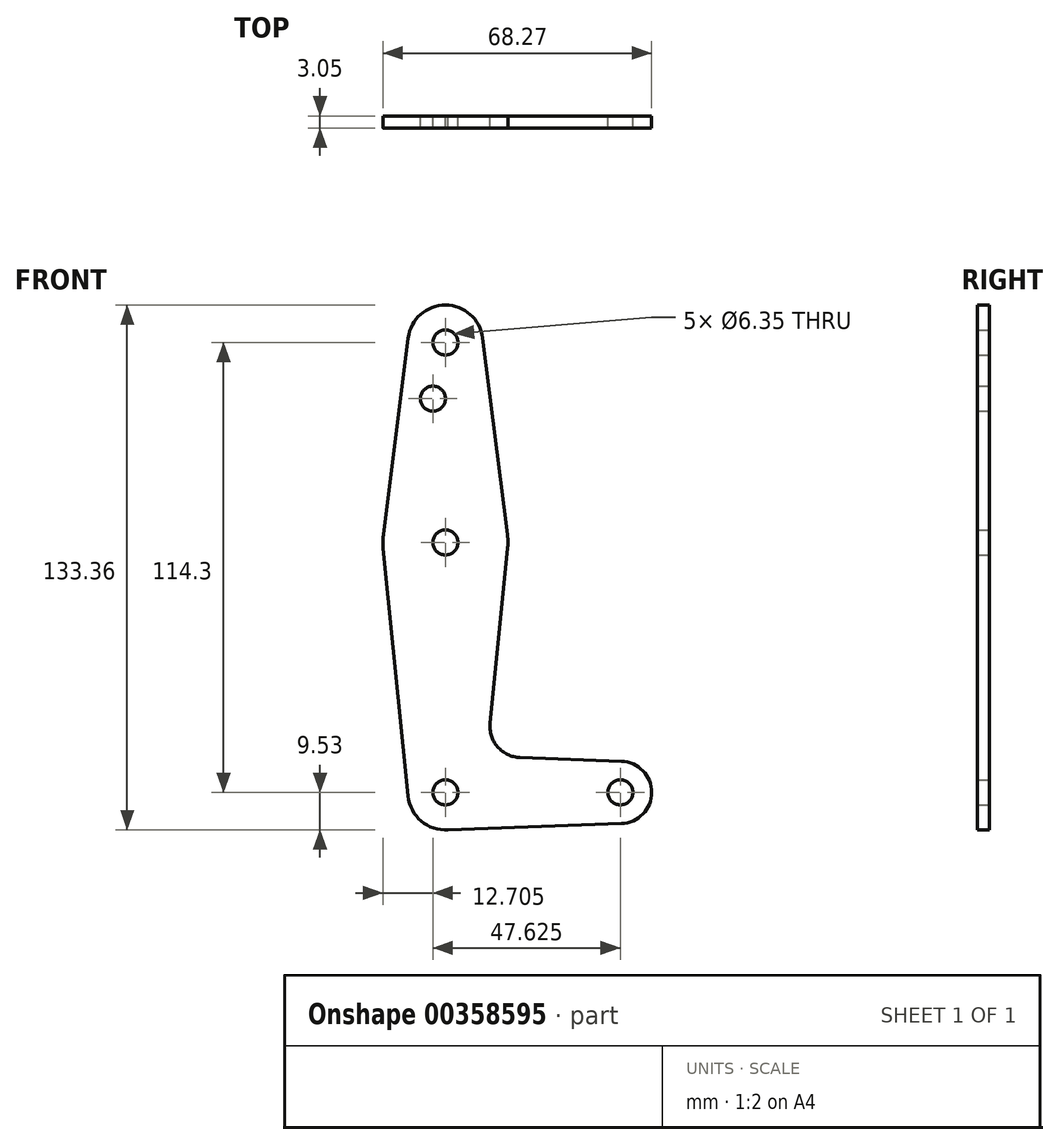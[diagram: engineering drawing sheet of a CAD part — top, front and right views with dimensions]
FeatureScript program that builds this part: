
annotation { "Feature Type Name" : "Feature", "Feature Type Description" : "" }
export const myFeature = defineFeature(function(context is Context, id is Id, definition is map)
    precondition{}
    {
        {
            var Q0;
            Q0=qCreatedBy(makeId("Front.planeOp"),FACE);
            var sketch = newSketch(context, id + "F0", { "sketchPlane" : qUnion([Q0])});
            skLineSegment(sketch, "E0", {"start": v(0, 114.3) * mm, "end": v(0, 0) * mm, "construction": true});
            skLineSegment(sketch, "E1", {"start": v(0, 0) * mm, "end": v(44.45, 0) * mm, "construction": true});
            skCircle(sketch, "E2", {"center": v(0, 114.3) * mm, "radius": 9.53 * mm});
            skCircle(sketch, "E3", {"center": v(0, 63.5) * mm, "radius": 15.88 * mm});
            skCircle(sketch, "E4", {"center": v(0, 0) * mm, "radius": 9.53 * mm});
            skCircle(sketch, "E5", {"center": v(44.45, 0) * mm, "radius": 7.94 * mm});
            skLineSegment(sketch, "E6", {"start": v(-9.45, 115.5) * mm, "end": v(-15.75, 65.48) * mm});
            skLineSegment(sketch, "E7", {"start": v(9.45, 115.5) * mm, "end": v(15.75, 65.48) * mm});
            skLineSegment(sketch, "E8", {"start": v(15.8, 61.91) * mm, "end": v(11.34, 17.6) * mm});
            skLineSegment(sketch, "E9", {"start": v(0, -9.52) * mm, "end": v(44.73, -7.93) * mm});
            skLineSegment(sketch, "E10", {"start": v(18.97, 8.85) * mm, "end": v(44.73, 7.93) * mm});
            skLineSegment(sketch, "E11", {"start": v(-9.48, -0.95) * mm, "end": v(-15.8, 61.91) * mm});
            skArc(sketch, "E12.filletArc", {"start": v(11.34, 17.6) * mm, "mid": v(13.26, 11.57) * mm, "end": v(18.97, 8.85) * mm});
            skCircle(sketch, "E13", {"center": v(0, 114.3) * mm, "radius": 3.18 * mm});
            skCircle(sketch, "E14", {"center": v(-3.17, 100.03) * mm, "radius": 3.18 * mm});
            skCircle(sketch, "E15", {"center": v(0, 63.5) * mm, "radius": 3.18 * mm});
            skCircle(sketch, "E16", {"center": v(0, 0) * mm, "radius": 3.18 * mm});
            skCircle(sketch, "E17", {"center": v(44.45, 0) * mm, "radius": 3.18 * mm});
            skSolve(sketch);
        }
        {
            var Q0;
            Q0 = qSketchRegion(id + "F0", true);
            extrude(context, id + "F1", {"entities" : qUnion([Q0]), "depth" : 3.05 * mm});
        }
    });
